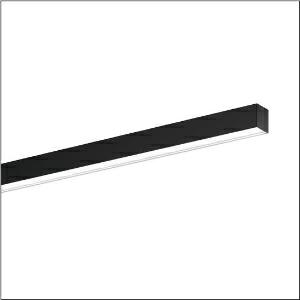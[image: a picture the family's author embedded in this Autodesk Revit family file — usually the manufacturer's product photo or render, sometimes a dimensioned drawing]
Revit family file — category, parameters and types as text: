
# Revit family: silica_r__21_51mx23tctab_c65d
name_source: partatom
category: Lighting Fixtures
units: mm (PartAtom-declared; Revit-internal decimal feet)

## family parameters
Cut with Voids When Loaded = No
Host = Face
Light Source = No
Part Type = Normal
Room Calculation Point = No
Round Connector Dimension = Use Diameter
Shared = No

## types (1)
- --- (1 x LED, 8070 lm, 81.1 W, 6500K)
    Apparent Load = 81 VA
    CIE Flux Codes = 78 96 99 100 100
    Color Rendering = 80
    Color Temperature = 6500K
    Default Elevation = 1800 mm
    Description = Silica® 21, office luminaire, primary optical cover: prismatic diffuser, of PMMA, CAT 2 (L<= 3000cd/m²), light emission: direct distribution, primary light characteristic: symmetric, installation type: surface-mounted, LED, rated luminous flux: 8.070lm, luminous efficacy: 95lm/W, light colour: 8tw, colour temperature: 2700..6500K, control gear: ECG DALI, with terminal, 3+2-pole, max. 2.5mm², mains connection: 220..240V, AC, 50/60Hz, rated input power: 85.1W, luminaire housing, of aluminium, jet black (RAL 9005), length: 3.004mm, width: 53mm, height: 53mm, protection rating (complete): IP20, insulation class (complete): insulation class I (protective earthing), certification: CE, permissible operating ambient temperature: 0..+35°C, standard: EN 50419, packaging unit: 1 piece
    Height = 0 mm  [stored 0 ft]
    Lamp = 1 x LED
    Lamp Light Flux = 8070 lm
    Lamp Power = 81.1 W
    Lamp count = 1
    Length = 3004 mm
    Luminous efficacy = 100 lm/W
    Manufacturer = Siteco
    ModVariant = No
    Model = 51MX23TCTAB
    Mounting Place = Ceiling
    Mounting Type = Recessed
    Number of Poles = 1
    OnlyDefault = Yes
    Power Factor = 1
    Product Name = Silica® 21
    Product group = office luminaire | ceiling recessed
    ProductGroupID = 401
    Protection Class = Protection class I
    Protection Degree = IP 20
    RLX_Detail_Level = 1
    RLX_Emergency_Light_Flux = 0 lm
    RLX_Emergency_Type = 0
    RLX_Emergency_Type_DB = No
    RlxData = <blob elided: 20369 chars, md5=f31c8a9a>
    Socket = socket
    Standby Power = 0 W
    System Light Flux = 8070 lm
    System Power = 81 W
    Type Comments = individual setting
    Type Image = l_1313584.jpg
    URL = http://relux.com
    VarID = @adj_089175
    Voltage = 0 V
    Weight = 0.00 kg
    Width = 53 mm

note: [stored X ft] marks values corroborated as IEEE doubles in the binary element streams (Revit-internal decimal feet)

## geometry (parser evidence)
native form markers: Blend x4, Sweep x10
no freeform markers — native parametric forms only
